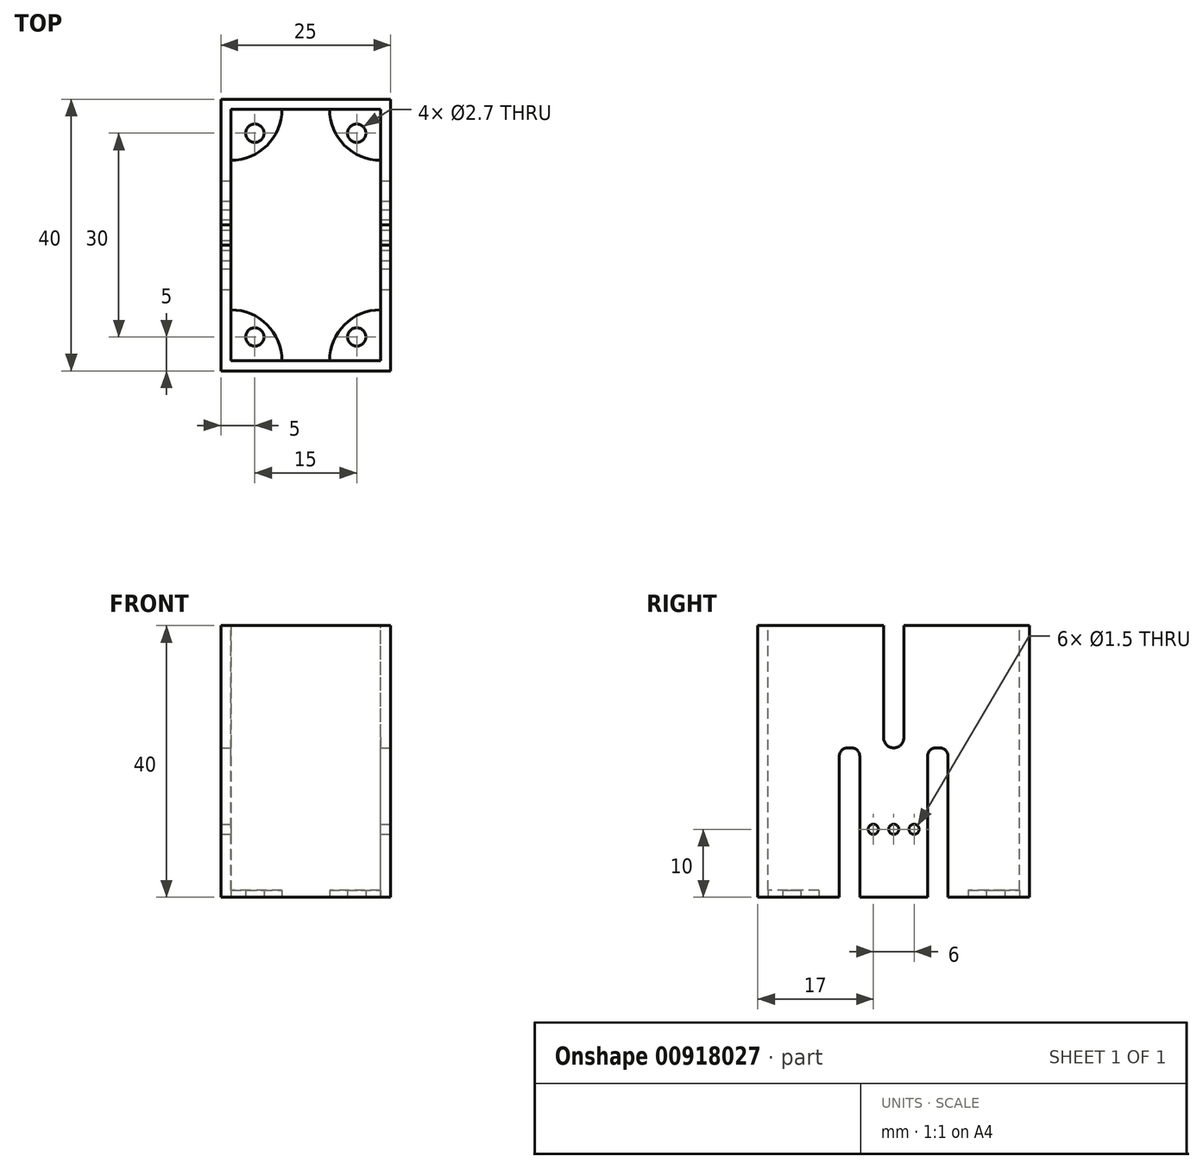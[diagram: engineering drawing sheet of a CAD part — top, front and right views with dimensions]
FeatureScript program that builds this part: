
annotation { "Feature Type Name" : "Feature", "Feature Type Description" : "" }
export const myFeature = defineFeature(function(context is Context, id is Id, definition is map)
    precondition{}
    {
        {
            var Q0;
            Q0=qCreatedBy(makeId("Top.planeOp"),FACE);
            var sketch = newSketch(context, id + "F0", { "sketchPlane" : qUnion([Q0])});
            skLineSegment(sketch, "E0.bottom", {"start": v(-12.5, 20) * mm, "end": v(12.5, 20) * mm});
            skLineSegment(sketch, "E0.top", {"start": v(-12.5, -20) * mm, "end": v(12.5, -20) * mm});
            skLineSegment(sketch, "E0.left", {"start": v(-12.5, 20) * mm, "end": v(-12.5, -20) * mm});
            skLineSegment(sketch, "E0.right", {"start": v(12.5, 20) * mm, "end": v(12.5, -20) * mm});
            skSolve(sketch);
        }
        {
            var Q0;
            Q0 = qSketchRegion(id + "F0", true);
            extrude(context, id + "F1", {"entities" : qUnion([Q0]), "depth" : 40 * mm, "offsetDistance" : 25 * mm});
        }
        {
            var Q0;
            Q0=makeQuery(id+"F1.opExtrude","CAP_FACE",FACE,{"disambiguationData":[OSD([sQuery(id+"F0.wireOp",EDGE,"E0.bottom"),sQuery(id+"F0.wireOp",EDGE,"E0.top"),sQuery(id+"F0.wireOp",EDGE,"E0.left"),sQuery(id+"F0.wireOp",EDGE,"E0.right")])],"isStart":false});
            var sketch = newSketch(context, id + "F2", { "sketchPlane" : qUnion([Q0])});
            skLineSegment(sketch, "E1.0", {"start": v(-11, 18.5) * mm, "end": v(-11, -18.5) * mm});
            skLineSegment(sketch, "E1.1", {"start": v(11, 18.5) * mm, "end": v(-11, 18.5) * mm});
            skLineSegment(sketch, "E1.2", {"start": v(11, -18.5) * mm, "end": v(11, 18.5) * mm});
            skLineSegment(sketch, "E1.3", {"start": v(-11, -18.5) * mm, "end": v(11, -18.5) * mm});
            skSolve(sketch);
        }
        {
            var Q0;
            Q0 = qSketchRegion(id + "F2", true);
            extrude(context, id + "F3", {"entities" : qUnion([Q0]), "operationType" : NewBodyOperationType.REMOVE, "endBound" : BoundingType.THROUGH_ALL, "oppositeDirection" : true, "depth" : 25 * mm, "offsetDistance" : 25 * mm});
        }
        {
            var Q0;
            Q0=makeQuery(id+"F1.opExtrude","CAP_FACE",FACE,{"disambiguationData":[OSD([sQuery(id+"F0.wireOp",EDGE,"E0.bottom"),sQuery(id+"F0.wireOp",EDGE,"E0.top"),sQuery(id+"F0.wireOp",EDGE,"E0.left"),sQuery(id+"F0.wireOp",EDGE,"E0.right")])],"isStart":true});
            var sketch = newSketch(context, id + "F4", { "sketchPlane" : qUnion([Q0])});
            skArc(sketch, "E2", {"start": v(-11, 11) * mm, "mid": v(-5.7, 13.2) * mm, "end": v(-3.5, 18.5) * mm});
            skArc(sketch, "E3", {"start": v(3.5, 18.5) * mm, "mid": v(5.7, 13.2) * mm, "end": v(11, 11) * mm});
            skArc(sketch, "E4", {"start": v(11, -11) * mm, "mid": v(5.7, -13.2) * mm, "end": v(3.5, -18.5) * mm});
            skArc(sketch, "E5", {"start": v(-3.5, -18.5) * mm, "mid": v(-5.7, -13.2) * mm, "end": v(-11, -11) * mm});
            skLineSegment(sketch, "E6", {"start": v(-11, 11) * mm, "end": v(-11, 18.5) * mm});
            skLineSegment(sketch, "E7", {"start": v(-11, 18.5) * mm, "end": v(-3.5, 18.5) * mm});
            skLineSegment(sketch, "E8", {"start": v(11, 18.5) * mm, "end": v(3.5, 18.5) * mm});
            skLineSegment(sketch, "E9", {"start": v(11, 18.5) * mm, "end": v(11, 11) * mm});
            skLineSegment(sketch, "E10", {"start": v(-11, -18.5) * mm, "end": v(-3.5, -18.5) * mm});
            skLineSegment(sketch, "E11", {"start": v(-11, -18.5) * mm, "end": v(-11, -11) * mm});
            skLineSegment(sketch, "E12", {"start": v(11, -18.5) * mm, "end": v(3.5, -18.5) * mm});
            skLineSegment(sketch, "E13", {"start": v(11, -18.5) * mm, "end": v(11, -11) * mm});
            skSolve(sketch);
        }
        {
            var Q0;
            Q0 = qSketchRegion(id + "F4", true);
            extrude(context, id + "F5", {"entities" : qUnion([Q0]), "operationType" : NewBodyOperationType.ADD, "oppositeDirection" : true, "depth" : 1 * mm, "offsetDistance" : 25 * mm});
        }
        {
            var Q0;
            Q0=makeQuery(id+"F5.boolean.opBoolean","MERGE",FACE,{"derivedFrom":[makeQuery(id+"F1.opExtrude","CAP_FACE",FACE,{"disambiguationData":[OSD([sQuery(id+"F0.wireOp",EDGE,"E0.bottom"),sQuery(id+"F0.wireOp",EDGE,"E0.top"),sQuery(id+"F0.wireOp",EDGE,"E0.left"),sQuery(id+"F0.wireOp",EDGE,"E0.right")])],"isStart":true}),makeQuery(id+"F5.opExtrude","CAP_FACE",FACE,{"disambiguationData":[OSD([sQuery(id+"F4.wireOp",EDGE,"E2"),sQuery(id+"F4.wireOp",EDGE,"E6"),sQuery(id+"F4.wireOp",EDGE,"E7")])],"isStart":true}),makeQuery(id+"F5.opExtrude","CAP_FACE",FACE,{"disambiguationData":[OSD([sQuery(id+"F4.wireOp",EDGE,"E3"),sQuery(id+"F4.wireOp",EDGE,"E8"),sQuery(id+"F4.wireOp",EDGE,"E9")])],"isStart":true}),makeQuery(id+"F5.opExtrude","CAP_FACE",FACE,{"disambiguationData":[OSD([sQuery(id+"F4.wireOp",EDGE,"E4"),sQuery(id+"F4.wireOp",EDGE,"E12"),sQuery(id+"F4.wireOp",EDGE,"E13")])],"isStart":true}),makeQuery(id+"F5.opExtrude","CAP_FACE",FACE,{"disambiguationData":[OSD([sQuery(id+"F4.wireOp",EDGE,"E5"),sQuery(id+"F4.wireOp",EDGE,"E10"),sQuery(id+"F4.wireOp",EDGE,"E11")])],"isStart":true})]});
            var sketch = newSketch(context, id + "F6", { "sketchPlane" : qUnion([Q0])});
            skLineSegment(sketch, "E14.bottom", {"start": v(-7.5, 15) * mm, "end": v(7.5, 15) * mm, "construction": true});
            skLineSegment(sketch, "E14.top", {"start": v(-7.5, -15) * mm, "end": v(7.5, -15) * mm, "construction": true});
            skLineSegment(sketch, "E14.left", {"start": v(-7.5, 15) * mm, "end": v(-7.5, -15) * mm, "construction": true});
            skLineSegment(sketch, "E14.right", {"start": v(7.5, 15) * mm, "end": v(7.5, -15) * mm, "construction": true});
            skCircle(sketch, "E15", {"center": v(7.5, 15) * mm, "radius": 1.35 * mm});
            skCircle(sketch, "E16", {"center": v(-7.5, 15) * mm, "radius": 1.35 * mm});
            skCircle(sketch, "E17", {"center": v(7.5, -15) * mm, "radius": 1.35 * mm});
            skCircle(sketch, "E18", {"center": v(-7.5, -15) * mm, "radius": 1.35 * mm});
            skSolve(sketch);
        }
        {
            var Q0;
            Q0 = qSketchRegion(id + "F6", true);
            extrude(context, id + "F7", {"entities" : qUnion([Q0]), "operationType" : NewBodyOperationType.REMOVE, "endBound" : BoundingType.THROUGH_ALL, "oppositeDirection" : true, "depth" : 25 * mm, "offsetDistance" : 25 * mm});
        }
        {
            var Q0;
            Q0=makeQuery(id+"F1.opExtrude","SWEPT_FACE",FACE,{"disambiguationData":[OSD([sQuery(id+"F0.wireOp",EDGE,"E0.right")])]});
            var sketch = newSketch(context, id + "F8", { "sketchPlane" : qUnion([Q0])});
            skArc(sketch, "E19", {"start": v(-1.5, 23.5) * mm, "mid": v(0, 22) * mm, "end": v(1.5, 23.5) * mm});
            skLineSegment(sketch, "E20", {"start": v(1.5, 23.5) * mm, "end": v(1.5, 40) * mm});
            skLineSegment(sketch, "E21", {"start": v(-1.5, 23.5) * mm, "end": v(-1.5, 40) * mm});
            skLineSegment(sketch, "E22.bottom", {"start": v(8, 0) * mm, "end": v(-8, 0) * mm});
            skLineSegment(sketch, "E22.top", {"start": v(5, 0) * mm, "end": v(-5, 0) * mm});
            skLineSegment(sketch, "E22.left", {"start": v(8, 0) * mm, "end": v(8, 0) * mm});
            skLineSegment(sketch, "E22.right", {"start": v(-8, 0) * mm, "end": v(-8, 0) * mm});
            skLineSegment(sketch, "E23.top", {"start": v(-8, 22) * mm, "end": v(-5, 22) * mm});
            skLineSegment(sketch, "E23.left", {"start": v(-8, 0) * mm, "end": v(-8, 22) * mm});
            skLineSegment(sketch, "E23.right", {"start": v(-5, 0) * mm, "end": v(-5, 22) * mm});
            skLineSegment(sketch, "E24.top", {"start": v(8, 22) * mm, "end": v(5, 22) * mm});
            skLineSegment(sketch, "E24.left", {"start": v(8, 0) * mm, "end": v(8, 22) * mm});
            skLineSegment(sketch, "E24.right", {"start": v(5, 0) * mm, "end": v(5, 22) * mm});
            skSolve(sketch);
        }
        {
            var Q0;
            Q0 = qSketchRegion(id + "F8", true);
            var Q1;
            Q1=makeQuery(id+"F8.imprint","IMPRINT",FACE,{"disambiguationData":[TD([[makeQuery(id+"F8.imprint","IMPRINT",EDGE,{"derivedFrom":sQuery(id+"F8.wireOp",EDGE,"E19")}),1.0]])]});
            extrude(context, id + "F9", {"entities" : qUnion([Q0, Q1]), "operationType" : NewBodyOperationType.REMOVE, "endBound" : BoundingType.THROUGH_ALL, "oppositeDirection" : true, "depth" : 25 * mm, "offsetDistance" : 25 * mm});
        }
        {
            var Q0;
            {var subQ0=sQuery(id+"F8.wireOp",EDGE,"E23.top");var subQ1=sQuery(id+"F8.wireOp",EDGE,"E23.right");Q0=makeQuery(id+"F9.boolean.opBoolean","COPY",EDGE,{"disambiguationData":[TD([makeQuery(id+"F1.opExtrude","SWEPT_FACE",FACE,{"disambiguationData":[OSD([sQuery(id+"F0.wireOp",EDGE,"E0.right")])]})])],"derivedFrom":makeQuery(id+"F9.opExtrude","SWEPT_EDGE",EDGE,{"disambiguationData":[OSD([subQ0,subQ1])]})});}
            var Q1;
            {var subQ0=sQuery(id+"F8.wireOp",EDGE,"E23.top");var subQ1=sQuery(id+"F8.wireOp",EDGE,"E23.left");Q1=makeQuery(id+"F9.boolean.opBoolean","COPY",EDGE,{"disambiguationData":[TD([makeQuery(id+"F1.opExtrude","SWEPT_FACE",FACE,{"disambiguationData":[OSD([sQuery(id+"F0.wireOp",EDGE,"E0.right")])]})])],"derivedFrom":makeQuery(id+"F9.opExtrude","SWEPT_EDGE",EDGE,{"disambiguationData":[OSD([subQ0,subQ1])]})});}
            var Q2;
            {var subQ0=sQuery(id+"F8.wireOp",EDGE,"E24.right");var subQ1=sQuery(id+"F8.wireOp",EDGE,"E24.top");Q2=makeQuery(id+"F9.boolean.opBoolean","COPY",EDGE,{"disambiguationData":[TD([makeQuery(id+"F1.opExtrude","SWEPT_FACE",FACE,{"disambiguationData":[OSD([sQuery(id+"F0.wireOp",EDGE,"E0.right")])]})])],"derivedFrom":makeQuery(id+"F9.opExtrude","SWEPT_EDGE",EDGE,{"disambiguationData":[OSD([subQ1,subQ0])]})});}
            var Q3;
            {var subQ0=sQuery(id+"F8.wireOp",EDGE,"E24.left");var subQ1=sQuery(id+"F8.wireOp",EDGE,"E24.top");Q3=makeQuery(id+"F9.boolean.opBoolean","COPY",EDGE,{"disambiguationData":[TD([makeQuery(id+"F1.opExtrude","SWEPT_FACE",FACE,{"disambiguationData":[OSD([sQuery(id+"F0.wireOp",EDGE,"E0.right")])]})])],"derivedFrom":makeQuery(id+"F9.opExtrude","SWEPT_EDGE",EDGE,{"disambiguationData":[OSD([subQ1,subQ0])]})});}
            var Q4;
            {var subQ0=sQuery(id+"F8.wireOp",EDGE,"E24.top");var subQ1=sQuery(id+"F8.wireOp",EDGE,"E24.left");Q4=makeQuery(id+"F9.boolean.opBoolean","COPY",EDGE,{"disambiguationData":[TD([makeQuery(id+"F1.opExtrude","SWEPT_FACE",FACE,{"disambiguationData":[OSD([sQuery(id+"F0.wireOp",EDGE,"E0.left")])]})])],"derivedFrom":makeQuery(id+"F9.opExtrude","SWEPT_EDGE",EDGE,{"disambiguationData":[OSD([subQ0,subQ1])]})});}
            var Q5;
            {var subQ0=sQuery(id+"F8.wireOp",EDGE,"E24.top");var subQ1=sQuery(id+"F8.wireOp",EDGE,"E24.right");Q5=makeQuery(id+"F9.boolean.opBoolean","COPY",EDGE,{"disambiguationData":[TD([makeQuery(id+"F1.opExtrude","SWEPT_FACE",FACE,{"disambiguationData":[OSD([sQuery(id+"F0.wireOp",EDGE,"E0.left")])]})])],"derivedFrom":makeQuery(id+"F9.opExtrude","SWEPT_EDGE",EDGE,{"disambiguationData":[OSD([subQ0,subQ1])]})});}
            var Q6;
            {var subQ0=sQuery(id+"F8.wireOp",EDGE,"E23.top");var subQ1=sQuery(id+"F8.wireOp",EDGE,"E23.right");Q6=makeQuery(id+"F9.boolean.opBoolean","COPY",EDGE,{"disambiguationData":[TD([makeQuery(id+"F1.opExtrude","SWEPT_FACE",FACE,{"disambiguationData":[OSD([sQuery(id+"F0.wireOp",EDGE,"E0.left")])]})])],"derivedFrom":makeQuery(id+"F9.opExtrude","SWEPT_EDGE",EDGE,{"disambiguationData":[OSD([subQ0,subQ1])]})});}
            var Q7;
            {var subQ0=sQuery(id+"F8.wireOp",EDGE,"E23.top");var subQ1=sQuery(id+"F8.wireOp",EDGE,"E23.left");Q7=makeQuery(id+"F9.boolean.opBoolean","COPY",EDGE,{"disambiguationData":[TD([makeQuery(id+"F1.opExtrude","SWEPT_FACE",FACE,{"disambiguationData":[OSD([sQuery(id+"F0.wireOp",EDGE,"E0.left")])]})])],"derivedFrom":makeQuery(id+"F9.opExtrude","SWEPT_EDGE",EDGE,{"disambiguationData":[OSD([subQ0,subQ1])]})});}
            fillet(context, id + "F10", {"entities" : qUnion([Q0, Q1, Q2, Q3, Q4, Q5, Q6, Q7]), "radius" : 1.2 * mm, "tangentPropagation" : true, "allowEdgeOverflow" : false});
        }
        {
            var Q0;
            Q0=makeQuery(id+"F1.opExtrude","SWEPT_FACE",FACE,{"disambiguationData":[OSD([sQuery(id+"F0.wireOp",EDGE,"E0.right")])]});
            var sketch = newSketch(context, id + "F11", { "sketchPlane" : qUnion([Q0])});
            skLineSegment(sketch, "E25", {"start": v(-10.24, 10) * mm, "end": v(11.61, 10) * mm, "construction": true});
            skCircle(sketch, "E26", {"center": v(-3, 10) * mm, "radius": 0.75 * mm});
            skCircle(sketch, "E27", {"center": v(0, 10) * mm, "radius": 0.75 * mm});
            skCircle(sketch, "E28", {"center": v(3, 10) * mm, "radius": 0.75 * mm});
            skSolve(sketch);
        }
        {
            var Q0;
            Q0 = qSketchRegion(id + "F11", true);
            extrude(context, id + "F12", {"entities" : qUnion([Q0]), "operationType" : NewBodyOperationType.REMOVE, "endBound" : BoundingType.THROUGH_ALL, "oppositeDirection" : true, "depth" : 25 * mm, "offsetDistance" : 25 * mm});
        }
    });
